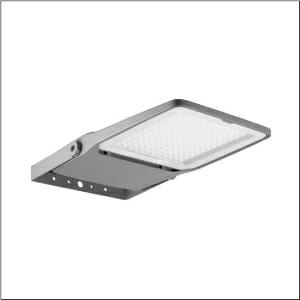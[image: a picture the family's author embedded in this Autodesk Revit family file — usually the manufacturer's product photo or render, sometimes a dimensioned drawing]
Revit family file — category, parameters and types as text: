
# Revit family: floodlight_fl_20_midi___pl61_5xa7682d1c2ac_a0aa
name_source: partatom
category: Lighting Fixtures
units: mm (PartAtom-declared; Revit-internal decimal feet)

## family parameters
Cut with Voids When Loaded = No
Host = Face
Light Source = No
Part Type = Normal
Room Calculation Point = No
Round Connector Dimension = Use Diameter
Shared = No

## types (1)
- --- (1 x LED 3000K / CRI = 80 (unbekannt), 14290 lm, 3000K)
    Apparent Load = 142 VA
    CIE Flux Codes = 33 65 98 100 100
    Color Rendering = 80
    Color Temperature = 3000K
    Default Elevation = 1800 mm
    Description = Floodlight FL 20 midi, floodlight, primary light control with lens, of plastic, primary optical cover: protective disc, of toughened safety glass, transparent, light distribution: PL61, light emission: direct distribution, primary light characteristic: asymmetric, installation type: surface-mounted, LED, High Power LED, rated luminous flux: 14.290lm, luminous efficacy: 101lm/W, light colour: 830, colour temperature: 3000K, control gear: ECG Plus, control: digital communication interface, time-dependent luminous flux control, flexible luminous flux parameterisation, power reduction, overheat protection, electronic power reduction, with terminal, 5-pole, max. 2.5mm², mains connection: 220..240V, AC, 50/60Hz, rated input power: 142W, LED unit, of diecast aluminium, powder-coated, Siteco® metallic grey (DB 702S), corrosivity category C5 mid according to DIN EN ISO 12944, incl. 1x M20 cable gland for cable Ø 6.5..12mm, length: 731mm, width: 450mm, height: 76mm, housing frame, of diecast aluminium, powder-coated, Siteco® metallic grey (DB 702S), wall fastening, of steel, powder-coated, Siteco® metallic grey (DB 702S), DALI, protection rating (complete): IP66, insulation class (complete): insulation class II (safety insulation), certification: CE, ENEC, VDE, protection symbol: D, permissible operating ambient temperature: -40..+40°C, permissible operating ambient temperature for outdoor applications: -40..+50°C, standard: DIN EN 12944, packaging unit: 1 piece

Light Distribution: PL61
    Height = 76 mm
    Lamp = 1 x LED 3000K / CRI >= 80 (unbekannt)
    Lamp Light Flux = 14290 lm
    Lamp count = 1
    Length = 731 mm
    Luminous efficacy = 101 lm/W
    Manufacturer = Siteco
    ModVariant = No
    Model = 5XA7682D1C2AC
    Mounting Place = Wall
    Mounting Type = Surface mounted
    Number of Poles = 1
    OnlyDefault = Yes
    Power Factor = 1
    Product Name = Floodlight FL 20 midi | PL61
    Product group = floodlight | wall mounted
    ProductGroupID = 2001
    Protection Class = Protection class II
    Protection Degree = IP 66
    RLX_Detail_Level = 1
    RLX_Emergency_Light_Flux = 0 lm
    RLX_Emergency_Type = 0
    RLX_Emergency_Type_DB = No
    RlxData = <blob elided: 92101 chars, md5=fa69f855>
    Socket = socket
    Standby Power = 0 W
    System Light Flux = 14290 lm
    System Power = 142 W
    Type Comments = factory setting: luminous flux: 100 % | dim-lin: 254 | 489 mA
    Type Image = l_1005944.jpg
    URL = http://relux.com
    VarID = @adj_147353
    Voltage = 0 V
    Weight = 0.00 kg
    Width = 450 mm

## geometry (parser evidence)
native form markers: Blend x4, Sweep x12
no freeform markers — native parametric forms only
